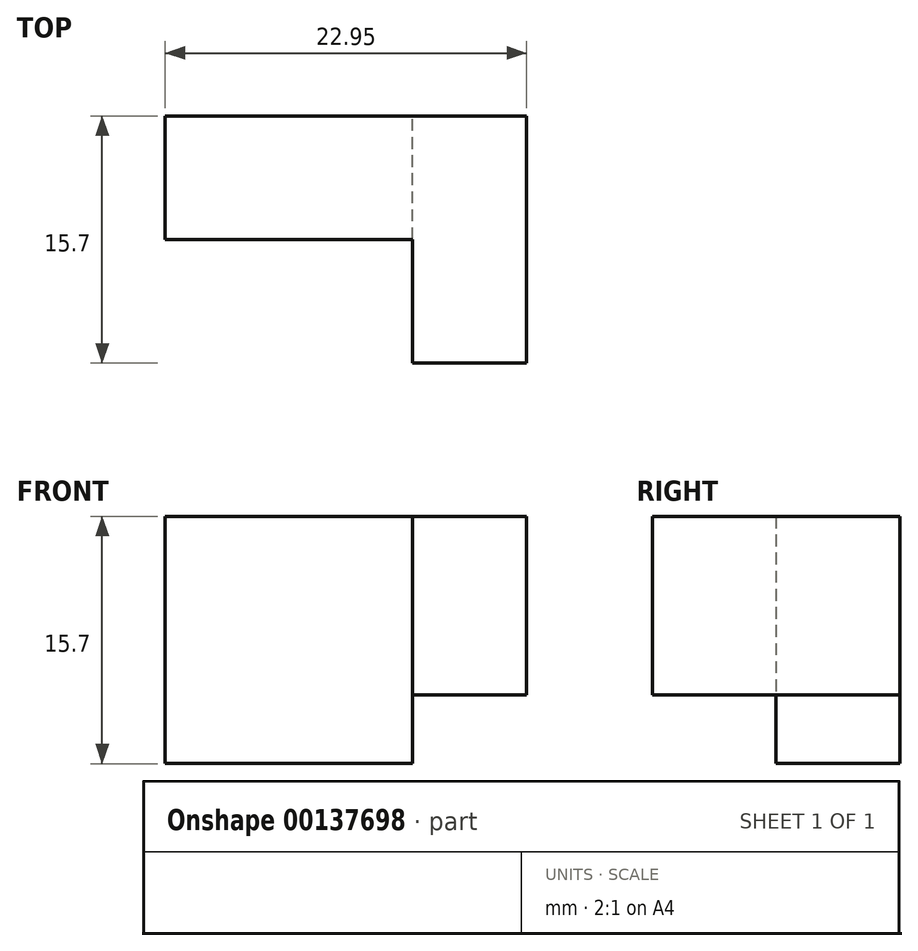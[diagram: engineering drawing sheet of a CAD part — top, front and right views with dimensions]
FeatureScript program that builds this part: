
annotation { "Feature Type Name" : "Feature", "Feature Type Description" : "" }
export const myFeature = defineFeature(function(context is Context, id is Id, definition is map)
    precondition{}
    {
        {
            var Q0;
            Q0=qCreatedBy(makeId("Front.planeOp"),FACE);
            var sketch = newSketch(context, id + "F0", { "sketchPlane" : qUnion([Q0])});
            skLineSegment(sketch, "E0.bottom", {"start": v(12.68, -3.88) * mm, "end": v(28.37, -3.88) * mm});
            skLineSegment(sketch, "E0.top", {"start": v(12.68, -19.58) * mm, "end": v(28.37, -19.58) * mm});
            skLineSegment(sketch, "E0.left", {"start": v(12.68, -3.88) * mm, "end": v(12.68, -19.58) * mm});
            skLineSegment(sketch, "E0.right", {"start": v(28.37, -3.88) * mm, "end": v(28.37, -19.58) * mm});
            skLineSegment(sketch, "E1.bottom", {"start": v(28.37, -3.88) * mm, "end": v(35.63, -3.88) * mm});
            skLineSegment(sketch, "E1.top", {"start": v(28.37, -15.2) * mm, "end": v(35.63, -15.2) * mm});
            skLineSegment(sketch, "E1.left", {"start": v(28.37, -3.88) * mm, "end": v(28.37, -15.2) * mm});
            skLineSegment(sketch, "E1.right", {"start": v(35.63, -3.88) * mm, "end": v(35.63, -15.2) * mm});
            skSolve(sketch);
        }
        {
            var Q0;
            Q0=makeQuery(id+"F0.imprint","IMPRINT",FACE,{"disambiguationData":[TD([[makeQuery(id+"F0.imprint","IMPRINT",EDGE,{"derivedFrom":sQuery(id+"F0.wireOp",EDGE,"E1.bottom")}),-1.0]])]});
            extrude(context, id + "F1", {"entities" : qUnion([Q0]), "depth" : 15.7 * mm});
        }
        {
            var Q0;
            Q0=makeQuery(id+"F0.imprint","IMPRINT",FACE,{"disambiguationData":[TD([[makeQuery(id+"F0.imprint","IMPRINT",EDGE,{"derivedFrom":sQuery(id+"F0.wireOp",EDGE,"E0.bottom")}),-1.0]])]});
            extrude(context, id + "F2", {"entities" : qUnion([Q0]), "operationType" : NewBodyOperationType.ADD, "depth" : 7.85 * mm});
        }
    });
